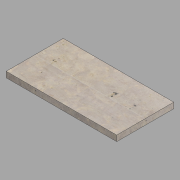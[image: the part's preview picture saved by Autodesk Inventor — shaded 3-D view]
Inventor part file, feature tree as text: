
AUTODESK INVENTOR PART (.ipt)
format: ipt  version: 2022.2 (Build 262287000, 287)  size: 108,544 bytes
history: native  units: in
note: dims shown in document units (in); Inventor stores cm internally (conversion verified against a paired STEP export)
features: extrude x1, sketch x1
ambient origin geometry x8: Origin, YZ Plane, XZ Plane, XY Plane, X Axis, Y Axis, Z Axis, Center Point
bodies: Solid1 (feature_tree)
feature tree (2):
  extrude  "Extrusion1"  Depth=10.0in
  sketch  "Sketch1"  dims[d0=19.375in d1=10.0in d2=1.0in d3=0.0in]
